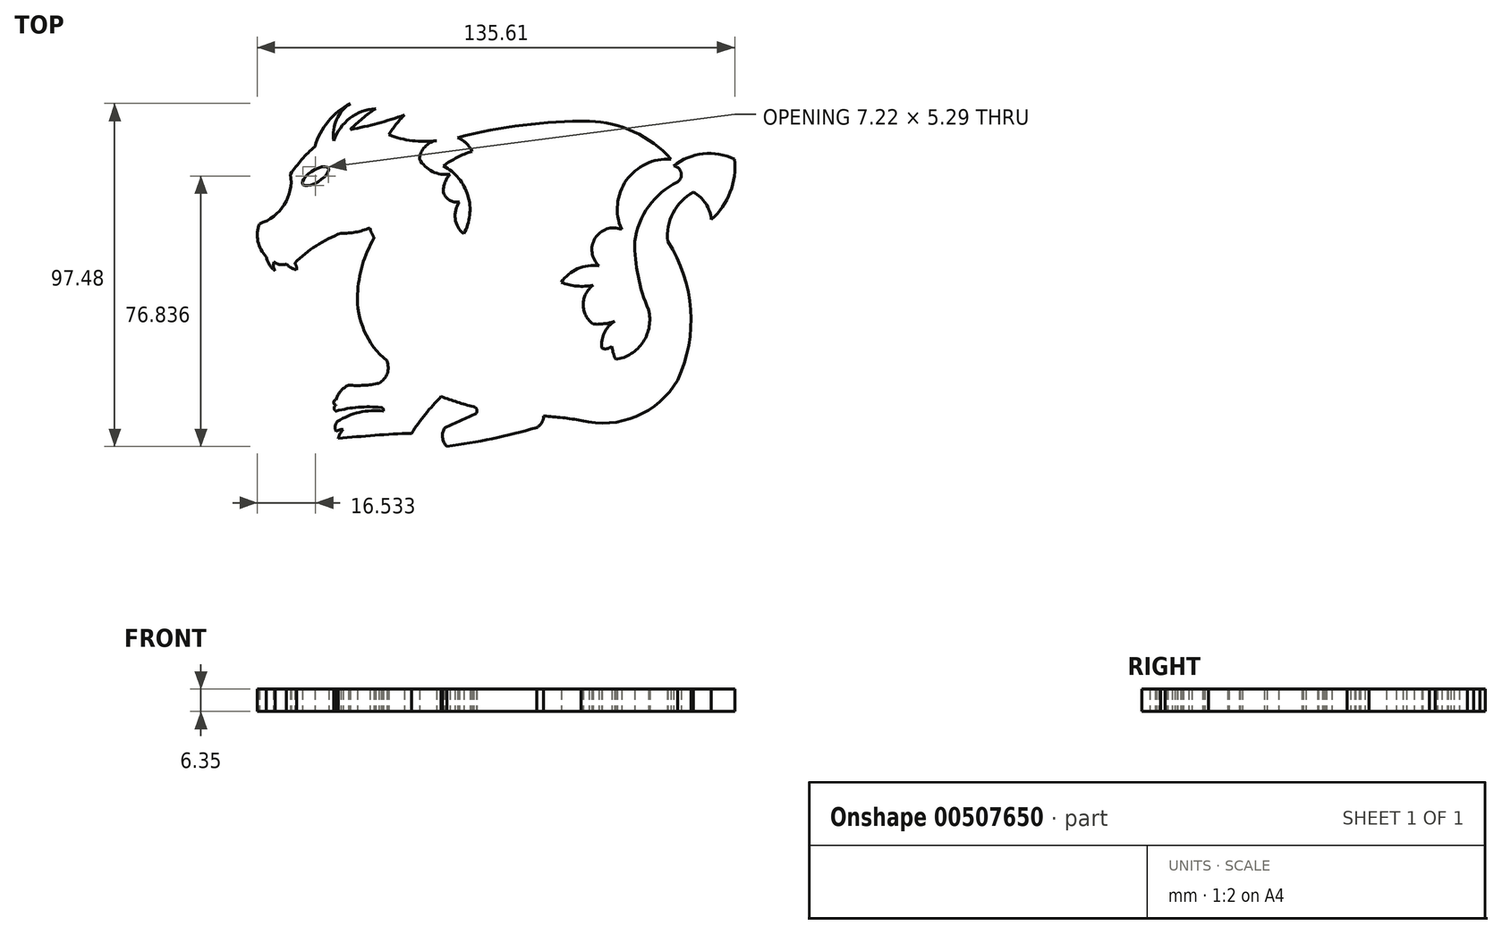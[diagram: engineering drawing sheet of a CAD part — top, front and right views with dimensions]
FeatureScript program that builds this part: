
annotation { "Feature Type Name" : "Feature", "Feature Type Description" : "" }
export const myFeature = defineFeature(function(context is Context, id is Id, definition is map)
    precondition{}
    {
        {
            var Q0;
            Q0=qCreatedBy(makeId("Top.planeOp"),FACE);
            var sketch = newSketch(context, id + "F0", { "sketchPlane" : qUnion([Q0])});
            skArc(sketch, "E0", {"start": v(-72.25, 23.98) * mm, "mid": v(-65.21, 29.39) * mm, "end": v(-63.4, 38.07) * mm});
            skArc(sketch, "E1", {"start": v(-56.5, 45.95) * mm, "mid": v(-60.22, 42.25) * mm, "end": v(-63.4, 38.07) * mm});
            skArc(sketch, "E2", {"start": v(-46.41, 58.16) * mm, "mid": v(-52.7, 53.08) * mm, "end": v(-56.5, 45.95) * mm});
            skArc(sketch, "E3", {"start": v(-46.41, 58.16) * mm, "mid": v(-50.34, 53.58) * mm, "end": v(-51.1, 47.6) * mm});
            skArc(sketch, "E4", {"start": v(-39.23, 56.72) * mm, "mid": v(-46.56, 53.97) * mm, "end": v(-51.1, 47.6) * mm});
            skArc(sketch, "E5", {"start": v(-39.23, 56.72) * mm, "mid": v(-42.98, 53.95) * mm, "end": v(-46.41, 50.78) * mm});
            skArc(sketch, "E6", {"start": v(-46.41, 50.78) * mm, "mid": v(-38.65, 52.5) * mm, "end": v(-31.07, 54.93) * mm});
            skArc(sketch, "E7", {"start": v(-31.07, 54.93) * mm, "mid": v(-33.43, 52.23) * mm, "end": v(-35.5, 49.3) * mm});
            skArc(sketch, "E8", {"start": v(-35.5, 49.3) * mm, "mid": v(-28.83, 47.6) * mm, "end": v(-21.96, 47.6) * mm});
            skArc(sketch, "E9", {"start": v(-21.96, 47.6) * mm, "mid": v(-25.29, 45.82) * mm, "end": v(-26.8, 42.35) * mm});
            skArc(sketch, "E10", {"start": v(-26.8, 42.35) * mm, "mid": v(-23.12, 38.84) * mm, "end": v(-18.09, 38.07) * mm});
            skArc(sketch, "E11", {"start": v(-18.09, 38.07) * mm, "mid": v(-19.58, 35.72) * mm, "end": v(-20.02, 32.96) * mm});
            skArc(sketch, "E12", {"start": v(-20.02, 32.96) * mm, "mid": v(-18.28, 30.69) * mm, "end": v(-15.46, 30.2) * mm});
            skArc(sketch, "E13", {"start": v(-15.46, 30.2) * mm, "mid": v(-16.65, 25.4) * mm, "end": v(-14.22, 21.08) * mm});
            skArc(sketch, "E14", {"start": v(-14.22, 21.08) * mm, "mid": v(-13.05, 31.97) * mm, "end": v(-20.02, 40.42) * mm});
            skArc(sketch, "E15", {"start": v(-11.87, 44.57) * mm, "mid": v(-16.11, 42.82) * mm, "end": v(-20.02, 40.42) * mm});
            skArc(sketch, "E16", {"start": v(-11.87, 44.57) * mm, "mid": v(-13.54, 46.88) * mm, "end": v(-15.93, 48.43) * mm});
            skArc(sketch, "E17", {"start": v(21.45, 53.1) * mm, "mid": v(2.6, 52.03) * mm, "end": v(-15.93, 48.43) * mm});
            skArc(sketch, "E18", {"start": v(44.61, 42.35) * mm, "mid": v(34.14, 50.13) * mm, "end": v(21.45, 53.1) * mm});
            skArc(sketch, "E19", {"start": v(44.61, 42.35) * mm, "mid": v(31.97, 36.33) * mm, "end": v(30.58, 22.4) * mm});
            skArc(sketch, "E20", {"start": v(30.58, 22.4) * mm, "mid": v(23.08, 19.87) * mm, "end": v(24.16, 12.03) * mm});
            skArc(sketch, "E21", {"start": v(24.16, 12.03) * mm, "mid": v(18.14, 11.2) * mm, "end": v(13.45, 7.33) * mm});
            skArc(sketch, "E22", {"start": v(13.45, 7.33) * mm, "mid": v(17.92, 6.25) * mm, "end": v(22.5, 6.5) * mm});
            skArc(sketch, "E23", {"start": v(22.5, 6.5) * mm, "mid": v(19.7, 0.98) * mm, "end": v(22.5, -4.55) * mm});
            skArc(sketch, "E24", {"start": v(22.5, -4.55) * mm, "mid": v(25.62, -4.45) * mm, "end": v(28.67, -3.76) * mm});
            skArc(sketch, "E25", {"start": v(28.67, -3.76) * mm, "mid": v(25.66, -7.02) * mm, "end": v(25.07, -11.42) * mm});
            skArc(sketch, "E26", {"start": v(25.07, -11.42) * mm, "mid": v(26.55, -11.53) * mm, "end": v(27.86, -10.81) * mm});
            skArc(sketch, "E27", {"start": v(27.86, -10.81) * mm, "mid": v(28.24, -12.75) * mm, "end": v(28.94, -14.6) * mm});
            skArc(sketch, "E28", {"start": v(28.94, -14.6) * mm, "mid": v(36.72, -9.6) * mm, "end": v(38.25, -0.5) * mm});
            skArc(sketch, "E29", {"start": v(34.3, 18.94) * mm, "mid": v(35.29, 9.02) * mm, "end": v(38.25, -0.5) * mm});
            skArc(sketch, "E30", {"start": v(46.53, 35.86) * mm, "mid": v(38.28, 28.94) * mm, "end": v(34.3, 18.94) * mm});
            skArc(sketch, "E31", {"start": v(46.53, 35.86) * mm, "mid": v(47.51, 38.53) * mm, "end": v(45.38, 40.42) * mm});
            skArc(sketch, "E32", {"start": v(62.64, 42.35) * mm, "mid": v(53.73, 43.9) * mm, "end": v(45.38, 40.42) * mm});
            skArc(sketch, "E33", {"start": v(56.06, 25.18) * mm, "mid": v(61.45, 32.97) * mm, "end": v(62.64, 42.35) * mm});
            skArc(sketch, "E34", {"start": v(56.06, 25.18) * mm, "mid": v(54.5, 29.72) * mm, "end": v(50.97, 32.96) * mm});
            skArc(sketch, "E35", {"start": v(50.97, 32.96) * mm, "mid": v(45.22, 27.05) * mm, "end": v(43.74, 18.94) * mm});
            skArc(sketch, "E36", {"start": v(46.53, -20.46) * mm, "mid": v(50.2, -0.4) * mm, "end": v(43.74, 18.94) * mm});
            skArc(sketch, "E37", {"start": v(19.16, -31.96) * mm, "mid": v(34.77, -30.79) * mm, "end": v(46.53, -20.46) * mm});
            skArc(sketch, "E38", {"start": v(19.16, -31.96) * mm, "mid": v(13.83, -31.16) * mm, "end": v(8.47, -30.68) * mm});
            skArc(sketch, "E39", {"start": v(6.5, -33.93) * mm, "mid": v(7.92, -32.57) * mm, "end": v(8.47, -30.68) * mm});
            skArc(sketch, "E40", {"start": v(-18.97, -39.32) * mm, "mid": v(-6.13, -37.12) * mm, "end": v(6.5, -33.93) * mm});
            skArc(sketch, "E41", {"start": v(-19.56, -33.93) * mm, "mid": v(-20.25, -36.73) * mm, "end": v(-18.97, -39.32) * mm});
            skArc(sketch, "E42", {"start": v(-19.56, -33.93) * mm, "mid": v(-15.06, -32) * mm, "end": v(-10.64, -29.89) * mm});
            skArc(sketch, "E43", {"start": v(-10.64, -29.89) * mm, "mid": v(-10.53, -28.75) * mm, "end": v(-11.43, -28.03) * mm});
            skArc(sketch, "E44", {"start": v(-20.63, -25.15) * mm, "mid": v(-16.07, -26.73) * mm, "end": v(-11.43, -28.03) * mm});
            skArc(sketch, "E45", {"start": v(-20.63, -25.15) * mm, "mid": v(-25.12, -30.13) * mm, "end": v(-29.03, -35.57) * mm});
            skArc(sketch, "E46", {"start": v(-29.03, -35.57) * mm, "mid": v(-39.47, -36.16) * mm, "end": v(-49.9, -37.09) * mm});
            skArc(sketch, "E47", {"start": v(-48.42, -34.45) * mm, "mid": v(-49.34, -35.67) * mm, "end": v(-49.9, -37.09) * mm});
            skArc(sketch, "E48", {"start": v(-48.42, -34.45) * mm, "mid": v(-49.5, -34.6) * mm, "end": v(-50.48, -35.08) * mm});
            skArc(sketch, "E49", {"start": v(-50.15, -32.24) * mm, "mid": v(-50.75, -33.61) * mm, "end": v(-50.48, -35.08) * mm});
            skArc(sketch, "E50", {"start": v(-37.11, -29.3) * mm, "mid": v(-43.89, -29.63) * mm, "end": v(-50.15, -32.24) * mm});
            skArc(sketch, "E51", {"start": v(-37.11, -29.3) * mm, "mid": v(-37.11, -28.6) * mm, "end": v(-37.73, -28.25) * mm});
            skArc(sketch, "E52", {"start": v(-37.73, -28.25) * mm, "mid": v(-44.15, -28.17) * mm, "end": v(-50.48, -29.3) * mm});
            skArc(sketch, "E53", {"start": v(-50.48, -27.57) * mm, "mid": v(-51.04, -28.43) * mm, "end": v(-50.48, -29.3) * mm});
            skArc(sketch, "E54", {"start": v(-50.48, -26.05) * mm, "mid": v(-51.18, -26.8) * mm, "end": v(-50.48, -27.57) * mm});
            skArc(sketch, "E55", {"start": v(-46.93, -21.9) * mm, "mid": v(-49.16, -23.58) * mm, "end": v(-50.48, -26.05) * mm});
            skArc(sketch, "E56", {"start": v(-46.93, -21.9) * mm, "mid": v(-42.6, -21.95) * mm, "end": v(-38.3, -21.36) * mm});
            skArc(sketch, "E57", {"start": v(-38.3, -21.36) * mm, "mid": v(-35.96, -18.59) * mm, "end": v(-36.1, -14.96) * mm});
            skArc(sketch, "E58", {"start": v(-44.4, 3.9) * mm, "mid": v(-42.45, -6.5) * mm, "end": v(-36.1, -14.96) * mm});
            skArc(sketch, "E59", {"start": v(-39.66, 19.94) * mm, "mid": v(-43.01, 12.21) * mm, "end": v(-44.4, 3.9) * mm});
            skArc(sketch, "E60", {"start": v(-40.87, 22.84) * mm, "mid": v(-40.4, 21.33) * mm, "end": v(-39.66, 19.94) * mm});
            skArc(sketch, "E61", {"start": v(-49.1, 21.32) * mm, "mid": v(-44.9, 21.59) * mm, "end": v(-40.87, 22.84) * mm});
            skArc(sketch, "E62", {"start": v(-49.1, 21.32) * mm, "mid": v(-56.12, 17.75) * mm, "end": v(-62.25, 12.79) * mm});
            skArc(sketch, "E63", {"start": v(-61.66, 10.88) * mm, "mid": v(-61.77, 11.9) * mm, "end": v(-62.25, 12.79) * mm});
            skArc(sketch, "E64", {"start": v(-64.56, 12.5) * mm, "mid": v(-63.25, 11.45) * mm, "end": v(-61.66, 10.88) * mm});
            skArc(sketch, "E65", {"start": v(-68.12, 13.1) * mm, "mid": v(-66.4, 12.4) * mm, "end": v(-64.56, 12.5) * mm});
            skArc(sketch, "E66", {"start": v(-68.12, 13.1) * mm, "mid": v(-68.26, 11.8) * mm, "end": v(-67.74, 10.6) * mm});
            skArc(sketch, "E67", {"start": v(-70.3, 14.58) * mm, "mid": v(-69.43, 12.33) * mm, "end": v(-67.74, 10.6) * mm});
            skArc(sketch, "E68", {"start": v(-72.25, 23.98) * mm, "mid": v(-72.67, 18.99) * mm, "end": v(-70.3, 14.58) * mm});
            skSolve(sketch);
        }
        {
            var Q0;
            Q0 = qSketchRegion(id + "F0", true);
            extrude(context, id + "F1", {"entities" : qUnion([Q0]), "depth" : 6.35 * mm});
        }
        {
            var Q0;
            Q0=makeQuery(id+"F1.opExtrude","CAP_FACE",FACE,{"disambiguationData":[OSD([sQuery(id+"F0.wireOp",EDGE,"E0"),sQuery(id+"F0.wireOp",EDGE,"E1"),sQuery(id+"F0.wireOp",EDGE,"E2"),sQuery(id+"F0.wireOp",EDGE,"E3"),sQuery(id+"F0.wireOp",EDGE,"E4"),sQuery(id+"F0.wireOp",EDGE,"E5"),sQuery(id+"F0.wireOp",EDGE,"E6"),sQuery(id+"F0.wireOp",EDGE,"E7"),sQuery(id+"F0.wireOp",EDGE,"E8"),sQuery(id+"F0.wireOp",EDGE,"E9"),sQuery(id+"F0.wireOp",EDGE,"E10"),sQuery(id+"F0.wireOp",EDGE,"E11"),sQuery(id+"F0.wireOp",EDGE,"E12"),sQuery(id+"F0.wireOp",EDGE,"E13"),sQuery(id+"F0.wireOp",EDGE,"E14"),sQuery(id+"F0.wireOp",EDGE,"E15"),sQuery(id+"F0.wireOp",EDGE,"E16"),sQuery(id+"F0.wireOp",EDGE,"E17"),sQuery(id+"F0.wireOp",EDGE,"E18"),sQuery(id+"F0.wireOp",EDGE,"E19"),sQuery(id+"F0.wireOp",EDGE,"E20"),sQuery(id+"F0.wireOp",EDGE,"E21"),sQuery(id+"F0.wireOp",EDGE,"E22"),sQuery(id+"F0.wireOp",EDGE,"E23"),sQuery(id+"F0.wireOp",EDGE,"E24"),sQuery(id+"F0.wireOp",EDGE,"E25"),sQuery(id+"F0.wireOp",EDGE,"E26"),sQuery(id+"F0.wireOp",EDGE,"E27"),sQuery(id+"F0.wireOp",EDGE,"E28"),sQuery(id+"F0.wireOp",EDGE,"E29"),sQuery(id+"F0.wireOp",EDGE,"E30"),sQuery(id+"F0.wireOp",EDGE,"E31"),sQuery(id+"F0.wireOp",EDGE,"E32"),sQuery(id+"F0.wireOp",EDGE,"E33"),sQuery(id+"F0.wireOp",EDGE,"E34"),sQuery(id+"F0.wireOp",EDGE,"E35"),sQuery(id+"F0.wireOp",EDGE,"E36"),sQuery(id+"F0.wireOp",EDGE,"E37"),sQuery(id+"F0.wireOp",EDGE,"E38"),sQuery(id+"F0.wireOp",EDGE,"E39"),sQuery(id+"F0.wireOp",EDGE,"E40"),sQuery(id+"F0.wireOp",EDGE,"E41"),sQuery(id+"F0.wireOp",EDGE,"E42"),sQuery(id+"F0.wireOp",EDGE,"E43"),sQuery(id+"F0.wireOp",EDGE,"E44"),sQuery(id+"F0.wireOp",EDGE,"E45"),sQuery(id+"F0.wireOp",EDGE,"E46"),sQuery(id+"F0.wireOp",EDGE,"E47"),sQuery(id+"F0.wireOp",EDGE,"E48"),sQuery(id+"F0.wireOp",EDGE,"E49"),sQuery(id+"F0.wireOp",EDGE,"E50"),sQuery(id+"F0.wireOp",EDGE,"E51"),sQuery(id+"F0.wireOp",EDGE,"E52"),sQuery(id+"F0.wireOp",EDGE,"E53"),sQuery(id+"F0.wireOp",EDGE,"E54"),sQuery(id+"F0.wireOp",EDGE,"E55"),sQuery(id+"F0.wireOp",EDGE,"E56"),sQuery(id+"F0.wireOp",EDGE,"E57"),sQuery(id+"F0.wireOp",EDGE,"E58"),sQuery(id+"F0.wireOp",EDGE,"E59"),sQuery(id+"F0.wireOp",EDGE,"E60"),sQuery(id+"F0.wireOp",EDGE,"E61"),sQuery(id+"F0.wireOp",EDGE,"E62"),sQuery(id+"F0.wireOp",EDGE,"E63"),sQuery(id+"F0.wireOp",EDGE,"E64"),sQuery(id+"F0.wireOp",EDGE,"E65"),sQuery(id+"F0.wireOp",EDGE,"E66"),sQuery(id+"F0.wireOp",EDGE,"E67"),sQuery(id+"F0.wireOp",EDGE,"E68")])],"isStart":false});
            var sketch = newSketch(context, id + "F2", { "sketchPlane" : qUnion([Q0])});
            skEllipse(sketch, "E69", {"center": v(-56.32, 37.52) * mm, "majorRadius": 4.28 * mm, "minorRadius": 1.7 * mm, "majorAxis": v(0.84, 0.54)});
            skSolve(sketch);
        }
        {
            var Q0;
            Q0=makeQuery(id+"F2.imprint","IMPRINT",FACE,{"disambiguationData":[TD([[makeQuery(id+"F2.imprint","IMPRINT",EDGE,{"derivedFrom":sQuery(id+"F2.wireOp",EDGE,"E69")}),1.0]])]});
            extrude(context, id + "F3", {"entities" : qUnion([Q0]), "operationType" : NewBodyOperationType.REMOVE, "oppositeDirection" : true, "depth" : 25.4 * mm});
        }
    });
